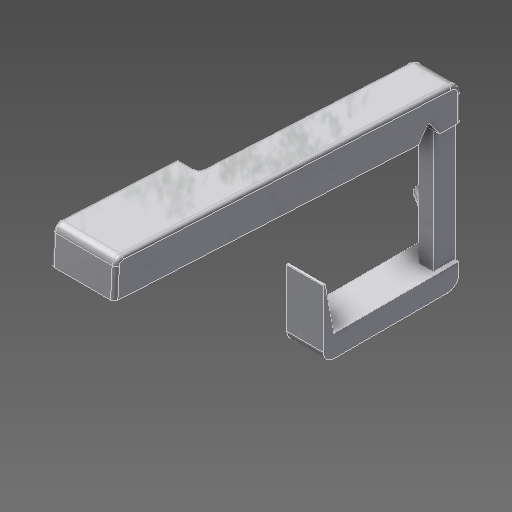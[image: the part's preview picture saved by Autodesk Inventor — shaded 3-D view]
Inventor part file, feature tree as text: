
AUTODESK INVENTOR PART (.ipt)
format: ipt  version: 2020 (Build 240168000, 168)  size: 324,608 bytes
history: native  units: mm
features: extrude x7, fillet x6, other x3, draft x1, chamfer x1
ambient origin geometry x8: Origin, YZ Plane, XZ Plane, XY Plane, X Axis, Y Axis, Z Axis, Center Point
bodies: Solid1 (feature_tree)
feature tree (18):
  other  "Key Sketch"
  extrude  "Upper Key"  Depth=10.0mm
  extrude  "Lower Key"  Depth=1.0mm
  other  "Hinge Cut Sketch"
  extrude  "Hinge Cut"  Depth=10.0mm TaperAngle=0.0deg
  extrude  "Hinge Cut 2"  Depth=3.0mm
  other  "Lever Sketch"
  extrude  "Vertical Lever"  Depth=3.0mm
  extrude  "Horizontal Lever"  Depth=33.6625mm
  extrude  "Spring Hook"  Depth=0.5mm
  draft  "FaceDraft3"
  chamfer  "Chamfer1"  Distance=3.0mm
  fillet  "Fillet9"  Radius=6.0mm
  fillet  "Fillet10"  Radius=4.0mm
  fillet  "Fillet5"  Radius=10.0mm
  fillet  "Fillet4"  [1 undecoded]
  fillet  "Fillet11"  Radius=3.0mm
  fillet  "Fillet14"  Radius=2.3mm
note: 1 required parameter value undecoded (feature->parameter linkage not recoverable at this tier; creation-order binding heuristic only, values carry confidence <= 0.55)
